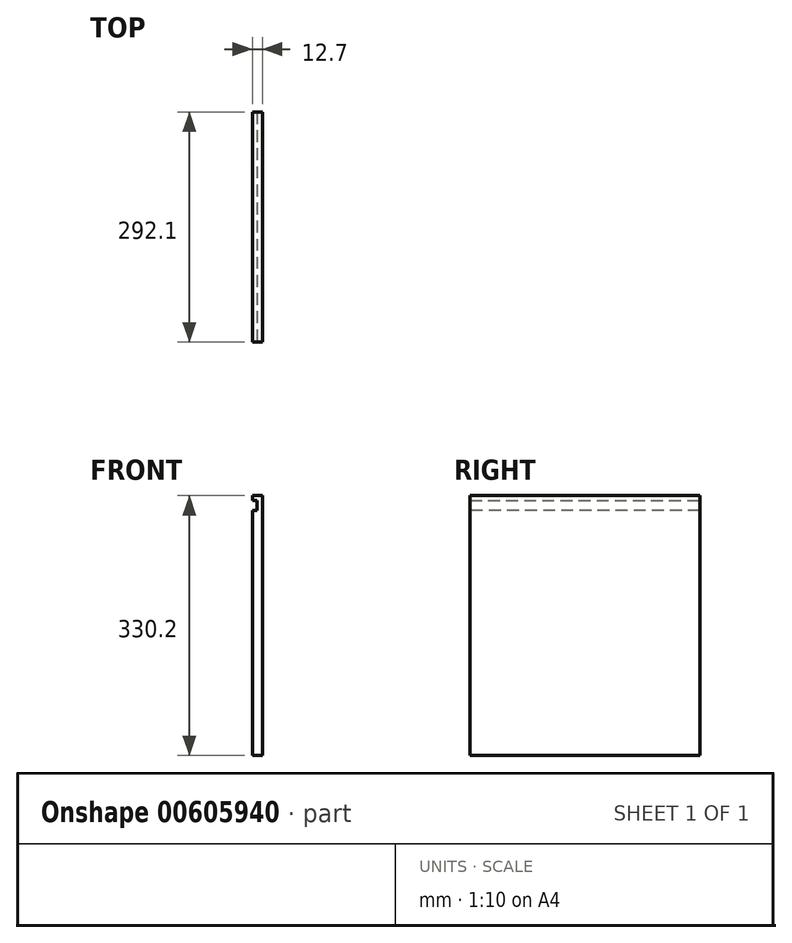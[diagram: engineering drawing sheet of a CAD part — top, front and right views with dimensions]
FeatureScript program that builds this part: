
annotation { "Feature Type Name" : "Feature", "Feature Type Description" : "" }
export const myFeature = defineFeature(function(context is Context, id is Id, definition is map)
    precondition{}
    {
        {
            var Q0;
            Q0=qCreatedBy(makeId("Right.planeOp"),FACE);
            var sketch = newSketch(context, id + "F0", { "sketchPlane" : qUnion([Q0])});
            skLineSegment(sketch, "E0.bottom", {"start": v(0, 0) * mm, "end": v(-292.1, 0) * mm});
            skLineSegment(sketch, "E0.top", {"start": v(0, 304.8) * mm, "end": v(-292.1, 304.8) * mm});
            skLineSegment(sketch, "E0.left", {"start": v(0, 0) * mm, "end": v(0, 304.8) * mm});
            skLineSegment(sketch, "E0.right", {"start": v(-292.1, 0) * mm, "end": v(-292.1, 304.8) * mm});
            skSolve(sketch);
        }
        {
            var Q0;
            Q0=makeQuery(id+"F0.imprint","IMPRINT",FACE,{"disambiguationData":[TD([[makeQuery(id+"F0.imprint","IMPRINT",EDGE,{"derivedFrom":sQuery(id+"F0.wireOp",EDGE,"E0.bottom")}),-1.0]])]});
            extrude(context, id + "F1", {"entities" : qUnion([Q0]), "depth" : 12.7 * mm, "offsetDistance" : 25.4 * mm});
        }
        {
            var Q0;
            Q0=qCreatedBy(makeId("Right.planeOp"),FACE);
            var sketch = newSketch(context, id + "F2", { "sketchPlane" : qUnion([Q0])});
            skLineSegment(sketch, "E1.bottom", {"start": v(0, 0) * mm, "end": v(-292.1, 0) * mm});
            skLineSegment(sketch, "E1.top", {"start": v(0, -25.4) * mm, "end": v(-292.1, -25.4) * mm});
            skLineSegment(sketch, "E1.left", {"start": v(0, 0) * mm, "end": v(0, -25.4) * mm});
            skLineSegment(sketch, "E1.right", {"start": v(-292.1, 0) * mm, "end": v(-292.1, -25.4) * mm});
            skSolve(sketch);
        }
        {
            var Q0;
            Q0=makeQuery(id+"F2.imprint","IMPRINT",FACE,{"disambiguationData":[TD([[makeQuery(id+"F2.imprint","IMPRINT",EDGE,{"derivedFrom":sQuery(id+"F2.wireOp",EDGE,"E1.bottom")}),1.0]])]});
            extrude(context, id + "F3", {"entities" : qUnion([Q0]), "operationType" : NewBodyOperationType.ADD, "depth" : 12.7 * mm, "offsetDistance" : 25.4 * mm});
        }
        {
            var Q0;
            Q0=makeQuery(id+"F3.boolean.opBoolean","MERGE",FACE,{"derivedFrom":[makeQuery(id+"F1.opExtrude","CAP_FACE",FACE,{"disambiguationData":[OSD([sQuery(id+"F0.wireOp",EDGE,"E0.bottom"),sQuery(id+"F0.wireOp",EDGE,"E0.top"),sQuery(id+"F0.wireOp",EDGE,"E0.left"),sQuery(id+"F0.wireOp",EDGE,"E0.right")])],"isStart":true}),makeQuery(id+"F3.opExtrude","CAP_FACE",FACE,{"disambiguationData":[OSD([sQuery(id+"F2.wireOp",EDGE,"E1.bottom"),sQuery(id+"F2.wireOp",EDGE,"E1.top"),sQuery(id+"F2.wireOp",EDGE,"E1.left"),sQuery(id+"F2.wireOp",EDGE,"E1.right")])],"isStart":true})]});
            var sketch = newSketch(context, id + "F4", { "sketchPlane" : qUnion([Q0])});
            skLineSegment(sketch, "E2", {"start": v(0, 304.8) * mm, "end": v(0, 298.45) * mm});
            skLineSegment(sketch, "E3", {"start": v(0, 298.45) * mm, "end": v(0, 285.75) * mm});
            skLineSegment(sketch, "E4", {"start": v(0, 285.75) * mm, "end": v(292.1, 285.75) * mm});
            skLineSegment(sketch, "E5", {"start": v(292.1, 285.75) * mm, "end": v(292.1, 298.45) * mm});
            skLineSegment(sketch, "E6", {"start": v(292.1, 298.45) * mm, "end": v(0, 298.45) * mm});
            skSolve(sketch);
        }
        {
            var Q0;
            Q0=makeQuery(id+"F4.imprint","IMPRINT",FACE,{"disambiguationData":[TD([[makeQuery(id+"F4.imprint","IMPRINT",EDGE,{"derivedFrom":sQuery(id+"F4.wireOp",EDGE,"E3")}),-1.0]])]});
            extrude(context, id + "F5", {"entities" : qUnion([Q0]), "operationType" : NewBodyOperationType.REMOVE, "oppositeDirection" : true, "depth" : 6.35 * mm, "offsetDistance" : 25.4 * mm});
        }
    });
